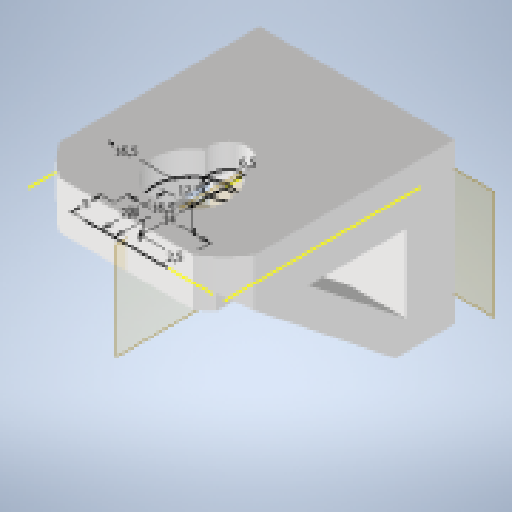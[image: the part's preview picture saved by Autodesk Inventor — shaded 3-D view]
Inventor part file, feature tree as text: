
AUTODESK INVENTOR PART (.ipt)
format: ipt  version: 2024 (Build 280153000, 153)  size: 715,264 bytes
history: native  units: mm
features: extrude x9, reference x6, projected_geometry x5, other x5, sketch x3, plane x2, mirror x1
ambient origin geometry x8: Origin, YZ Plane, XZ Plane, XY Plane, X Axis, Y Axis, Z Axis, Center Point
bodies: Solid1 (feature_tree)
feature tree (31):
  plane  "Work Plane1"
  extrude  "Extrusion1"  Depth=4.0mm
  extrude  "Extrusion7"  Depth=11.0mm
  extrude  "Extrusion9"  Depth=10.0mm
  extrude  "Extrusion8"  Depth=10.0mm
  extrude  "Extrusion10"  Depth=10.0mm
  extrude  "Extrusion11"  Depth=10.0mm
  plane  "Work Plane3"
  mirror  "Mirror3"
  extrude  "Extrusion12"  Depth=10.0mm
  extrude  "Extrusion13"  Depth=10.0mm
  extrude  "Extrusion15"  Depth=10.0mm
  reference  "Reference1"
  reference  "Reference2"
  reference  "Reference3"
  reference  "Reference4"
  reference  "Reference5"
  reference  "Reference6"
  projected_geometry  "Projected Loop4"
  projected_geometry  "Projected Loop5"
  sketch  "Sketch15"  dims[d0=6.0mm d1=0.0mm d42=4.0mm]
  projected_geometry  "Projected Loop6"
  sketch  "Sketch16"  dims[d43=33.0mm d44=0.0mm d46=11.0mm]
  projected_geometry  "Projected Loop7"
  projected_geometry  "Projected Loop8"
  sketch  "Sketch18"  dims[d47=12.5mm d48=6.5mm d49=14.0mm d50=5.0mm d51=2.5mm d52=16.5mm d53=2.5mm d54=16.5mm d55=4.0mm d56=0.0mm d57=0.0mm d58=0.0mm d59=3.0mm d60=3.0mm d61=20.0mm d62=0.0mm d65=4.0mm d66=0.0mm d67=-16.5mm d89=10.0mm d90=5.0mm d91=10.0mm d92=0.0mm d93=0.0mm d94=0.0mm d111=40.0mm d112=22.500017mm d113=10.0mm d114=0.0mm d30=0.5mm d31=0.872665mm d32=0.5mm d33=0.872665mm d95=0.5mm d96=0.872665mm d107=0.0mm d108=0.0mm d109=0.0mm d110=0.0mm]
  other  "<userpath> windows\Documents\Inventor\Robotska_roka\Assembly4.iam"
  other  "Assembly4.iam"
  other  "SG90 - Micro Servo 9g - Tower Pro:1"
  other  "SG90 - Micro Servo 9g - Tower Pro.4"
  other  "roka2:1"
